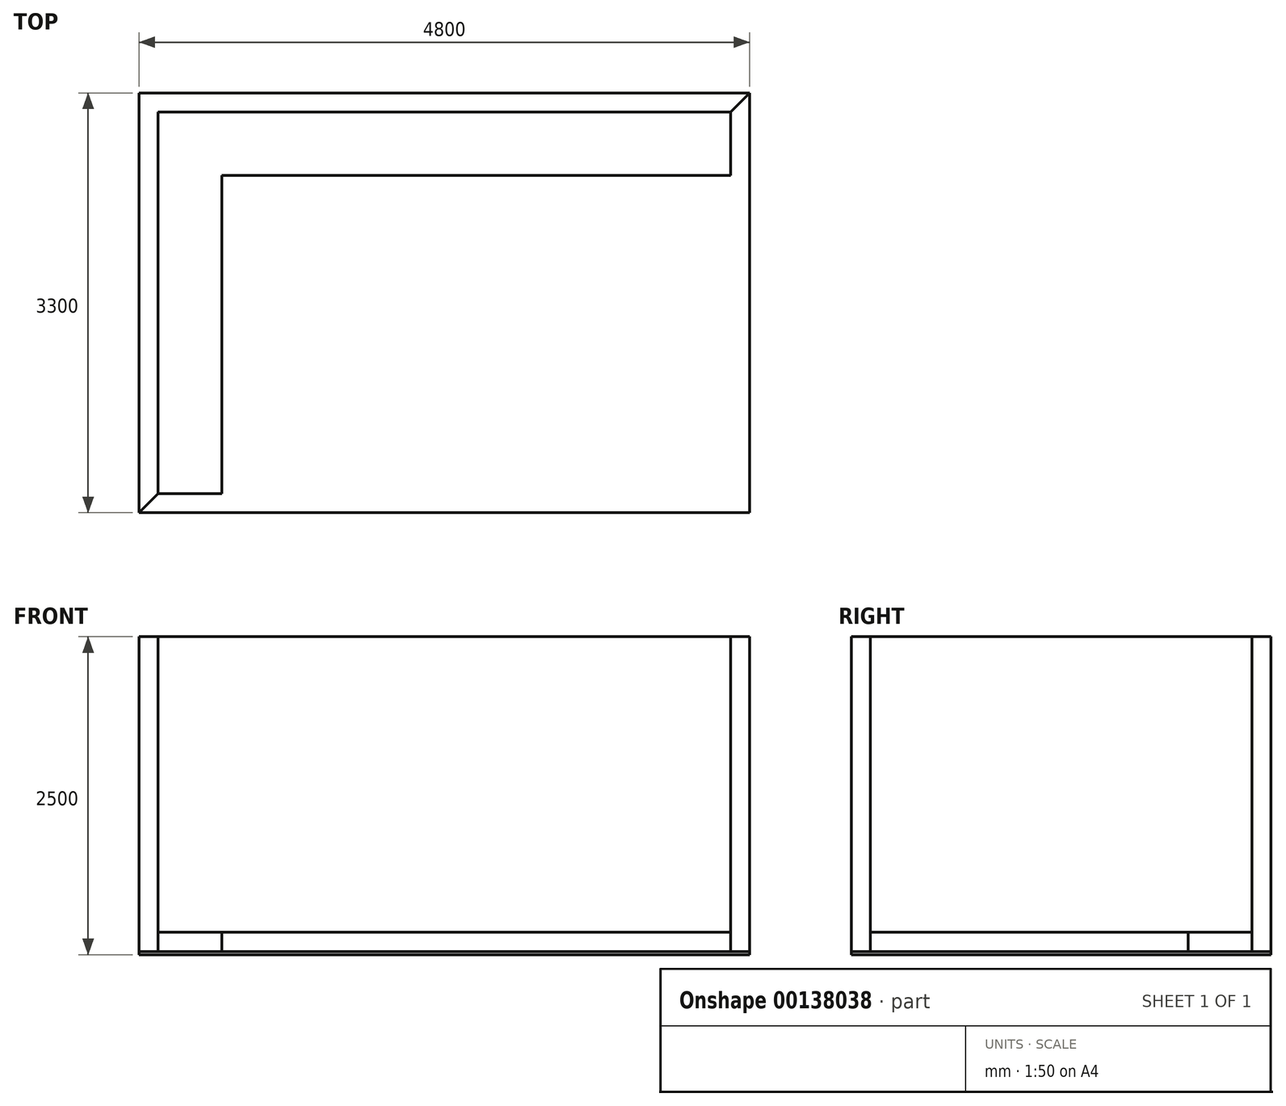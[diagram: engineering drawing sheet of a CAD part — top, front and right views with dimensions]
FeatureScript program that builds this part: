
annotation { "Feature Type Name" : "Feature", "Feature Type Description" : "" }
export const myFeature = defineFeature(function(context is Context, id is Id, definition is map)
    precondition{}
    {
        {
            var Q0;
            Q0=qCreatedBy(makeId("Top.planeOp"),FACE);
            var sketch = newSketch(context, id + "F0", { "sketchPlane" : qUnion([Q0])});
            skLineSegment(sketch, "E0.bottom", {"start": v(-2246.39, 1679.27) * mm, "end": v(2253.61, 1679.27) * mm});
            skLineSegment(sketch, "E0.left", {"start": v(-2246.39, 1679.27) * mm, "end": v(-2246.39, -1320.73) * mm});
            skLineSegment(sketch, "E1.0", {"start": v(-2396.39, 1829.27) * mm, "end": v(2403.61, 1829.27) * mm});
            skLineSegment(sketch, "E1.1", {"start": v(-2396.39, 1829.27) * mm, "end": v(-2396.39, -1470.73) * mm});
            skLineSegment(sketch, "E1.2", {"start": v(-2396.39, -1470.73) * mm, "end": v(2403.61, -1470.73) * mm});
            skLineSegment(sketch, "E1.3", {"start": v(2403.61, 1829.27) * mm, "end": v(2403.61, -1470.73) * mm});
            skLineSegment(sketch, "E2", {"start": v(-2246.39, -1320.73) * mm, "end": v(-2396.39, -1470.73) * mm});
            skLineSegment(sketch, "E3", {"start": v(2253.61, 1679.27) * mm, "end": v(2403.61, 1829.27) * mm});
            skSolve(sketch);
        }
        {
            var Q0;
            Q0=makeQuery(id+"F0.imprint","IMPRINT",FACE,{"disambiguationData":[TD([[makeQuery(id+"F0.imprint","IMPRINT",EDGE,{"derivedFrom":sQuery(id+"F0.wireOp",EDGE,"E0.bottom")}),1.0]])]});
            extrude(context, id + "F1", {"entities" : qUnion([Q0]), "depth" : 2500 * mm});
        }
        {
            var Q0;
            Q0=makeQuery(id+"F0.imprint","IMPRINT",FACE,{"disambiguationData":[TD([[makeQuery(id+"F0.imprint","IMPRINT",EDGE,{"derivedFrom":sQuery(id+"F0.wireOp",EDGE,"E0.bottom")}),-1.0]])]});
            extrude(context, id + "F2", {"entities" : qUnion([Q0]), "operationType" : NewBodyOperationType.ADD, "depth" : 25 * mm});
        }
        {
            var Q0;
            Q0=makeQuery(id+"F1.opExtrude","SWEPT_FACE",FACE,{"disambiguationData":[OSD([sQuery(id+"F0.wireOp",EDGE,"E0.left")])]});
            var sketch = newSketch(context, id + "F3", { "sketchPlane" : qUnion([Q0])});
            skLineSegment(sketch, "E4.bottom", {"start": v(1679.27, 25) * mm, "end": v(-1320.73, 25) * mm});
            skLineSegment(sketch, "E4.top", {"start": v(1679.27, 175) * mm, "end": v(-1320.73, 175) * mm});
            skLineSegment(sketch, "E4.left", {"start": v(1679.27, 25) * mm, "end": v(1679.27, 175) * mm});
            skLineSegment(sketch, "E4.right", {"start": v(-1320.73, 25) * mm, "end": v(-1320.73, 175) * mm});
            skSolve(sketch);
        }
        {
            var Q0;
            Q0=makeQuery(id+"F1.opExtrude","SWEPT_FACE",FACE,{"disambiguationData":[OSD([sQuery(id+"F0.wireOp",EDGE,"E0.bottom")])]});
            var sketch = newSketch(context, id + "F4", { "sketchPlane" : qUnion([Q0])});
            skLineSegment(sketch, "E5.bottom", {"start": v(-2246.39, 25) * mm, "end": v(2253.61, 25) * mm});
            skLineSegment(sketch, "E5.top", {"start": v(-2246.39, 175) * mm, "end": v(2253.61, 175) * mm});
            skLineSegment(sketch, "E5.left", {"start": v(-2246.39, 25) * mm, "end": v(-2246.39, 175) * mm});
            skLineSegment(sketch, "E5.right", {"start": v(2253.61, 25) * mm, "end": v(2253.61, 175) * mm});
            skSolve(sketch);
        }
        {
            var Q0;
            Q0=makeQuery(id+"F4.imprint","IMPRINT",FACE,{"disambiguationData":[TD([[makeQuery(id+"F4.imprint","IMPRINT",EDGE,{"derivedFrom":sQuery(id+"F4.wireOp",EDGE,"E5.bottom")}),1.0]])]});
            extrude(context, id + "F5", {"entities" : qUnion([Q0]), "operationType" : NewBodyOperationType.ADD, "depth" : 500 * mm});
        }
        {
            var Q0;
            Q0=makeQuery(id+"F3.imprint","IMPRINT",FACE,{"disambiguationData":[TD([[makeQuery(id+"F3.imprint","IMPRINT",EDGE,{"derivedFrom":sQuery(id+"F3.wireOp",EDGE,"E4.bottom")}),-1.0]])]});
            extrude(context, id + "F6", {"entities" : qUnion([Q0]), "operationType" : NewBodyOperationType.ADD, "depth" : 500 * mm});
        }
    });
